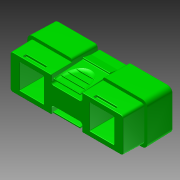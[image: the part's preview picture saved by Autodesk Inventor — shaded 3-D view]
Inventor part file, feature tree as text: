
AUTODESK INVENTOR PART (.ipt)
format: ipt  version: 2015 (Build 190159000, 159)  size: 1,795,072 bytes
history: native  units: in
note: dims shown in document units (in); Inventor stores cm internally (conversion verified against a paired STEP export)
features: extrude x8, fillet x8, sketch x7, draft x4, mirror x2, projected_geometry x1
ambient origin geometry x8: Origin, YZ Plane, XZ Plane, XY Plane, X Axis, Y Axis, Z Axis, Center Point
bodies: Solid1 (feature_tree)
feature tree (30):
  sketch  "Sketch1"  dims[d0=0.34in d1=0.8in]
  extrude  "Extrusion1"  Depth=0.8in
  extrude  "Extrusion2"  Depth=0.2975in
  extrude  "Extrusion3"  Depth=0.06in
  draft  "FaceDraft1"
  draft  "FaceDraft2"
  extrude  "Extrusion4"  Depth=0.5in TaperAngle=0.0deg
  extrude  "Extrusion5"  Depth=0.15in
  fillet  "Fillet1"  Radius=0.33in
  fillet  "Fillet2"  Radius=0.0069in
  extrude  "Extrusion6"  Depth=0.17in
  draft  "FaceDraft3"
  fillet  "Fillet3"  Radius=0.17in
  fillet  "Fillet4"  Radius=0.04in
  fillet  "Fillet5"  Radius=0.09in
  extrude  "Extrusion7"  Depth=0.03in
  extrude  "Extrusion8"  Depth=0.33in
  draft  "FaceDraft4"
  fillet  "Fillet6"  Radius=0.0206in
  fillet  "Fillet7"  Radius=0.0412in
  fillet  "Fillet8"  Radius=0.2625in
  mirror  "Mirror1"
  mirror  "Mirror2"
  sketch  "Sketch2"  dims[d2=0.175in d3=0.2975in]
  sketch  "Sketch3"  dims[d4=0.06in d5=0.06in]
  sketch  "Sketch4"  dims[d6=0.4in d7=0.0in d8=0.5in d9=0.0in]
  projected_geometry  "Projected Loop1"
  sketch  "Sketch5"  dims[d11=0.8in d12=0.15in d13=0.33in d14=0.0in d15=0.0069in]
  sketch  "Sketch6"  dims[d16=0.0069in d17=0.17in d18=0.17in d19=0.04in d20=0.09in]
  sketch  "Sketch7"  dims[d21=0.84in d22=0.03in d24=0.33in d25=0.0206in d26=0.0412in d27=0.2625in d28=0.0in d31=0.25in d32=0.1in d33=0.2in d34=0.6174in d35=0.01in d36=0.02in d37=0.0in d38=0.05in d39=0.185in d40=0.02in d41=0.125in d42=0.24in d43=0.36in d44=0.26in d45=0.01in d46=0.01in d47=0.0in d48=0.0137in d49=0.4in d50=0.06in d51=0.48in d52=0.3in d53=0.04in d54=0.0in d55=0.2375in d56=0.47in d57=0.186in d58=0.47in d59=0.0in d60=0.0069in d61=0.05in d62=0.01in d63=0.005in d64=0.1in]
